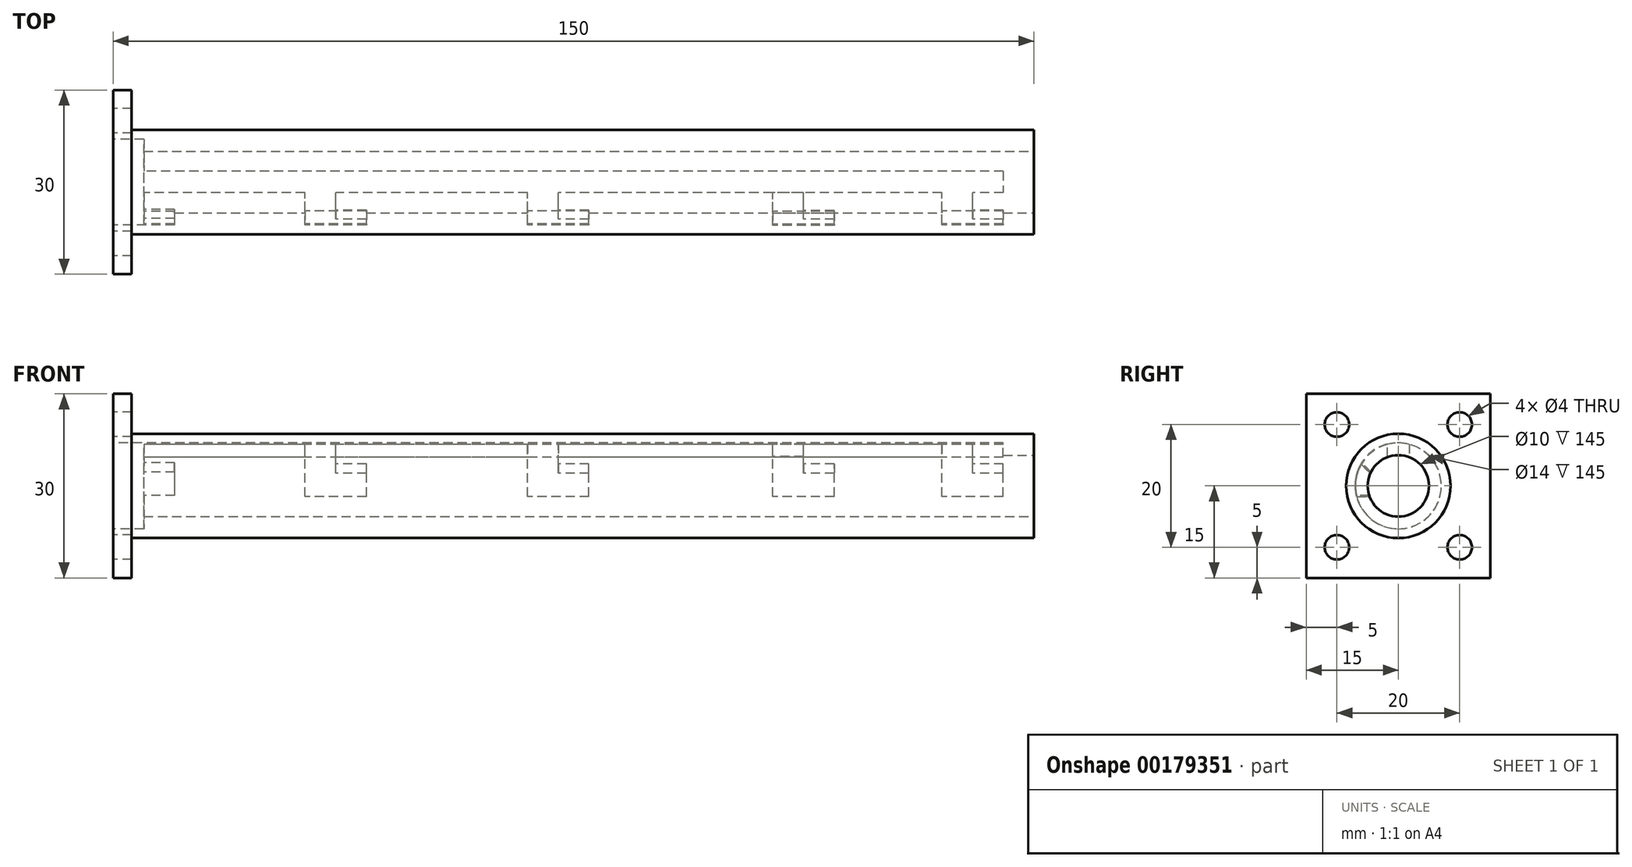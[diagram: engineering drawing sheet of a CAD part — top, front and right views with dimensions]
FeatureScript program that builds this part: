
annotation { "Feature Type Name" : "Feature", "Feature Type Description" : "" }
export const myFeature = defineFeature(function(context is Context, id is Id, definition is map)
    precondition{}
    {
        {
            var Q0;
            Q0=qCreatedBy(makeId("Right.planeOp"),FACE);
            var sketch = newSketch(context, id + "F0", { "sketchPlane" : qUnion([Q0])});
            skCircle(sketch, "E0", {"center": v(0, 0) * mm, "radius": 8.5 * mm});
            skCircle(sketch, "E1", {"center": v(0, 0) * mm, "radius": 7 * mm});
            skSolve(sketch);
        }
        {
            var Q0;
            Q0=makeQuery(id+"F0.imprint","IMPRINT",FACE,{"disambiguationData":[TD([[makeQuery(id+"F0.imprint","IMPRINT",EDGE,{"derivedFrom":sQuery(id+"F0.wireOp",EDGE,"E0")}),1.0]])]});
            extrude(context, id + "F1", {"entities" : qUnion([Q0]), "depth" : 150 * mm});
        }
        {
            var Q0;
            Q0=makeQuery(id+"F1.opExtrude","CAP_FACE",FACE,{"disambiguationData":[OSD([sQuery(id+"F0.wireOp",EDGE,"E0"),sQuery(id+"F0.wireOp",EDGE,"E1")])],"isStart":false});
            var sketch = newSketch(context, id + "F2", { "sketchPlane" : qUnion([Q0])});
            skCircle(sketch, "E2", {"center": v(0, 0) * mm, "radius": 5 * mm});
            skSolve(sketch);
        }
        {
            var Q0;
            Q0=makeQuery(id+"F2.imprint","IMPRINT",FACE,{"disambiguationData":[TD([[makeQuery(id+"F2.imprint","IMPRINT",EDGE,{"derivedFrom":sQuery(id+"F2.wireOp",EDGE,"E2")}),-1.0]])]});
            extrude(context, id + "F3", {"entities" : qUnion([Q0]), "operationType" : NewBodyOperationType.ADD, "oppositeDirection" : true, "depth" : 145 * mm});
        }
        {
            var Q0;
            Q0=makeQuery(id+"F1.opExtrude","CAP_FACE",FACE,{"disambiguationData":[OSD([sQuery(id+"F0.wireOp",EDGE,"E0"),sQuery(id+"F0.wireOp",EDGE,"E1")])],"isStart":true});
            var sketch = newSketch(context, id + "F4", { "sketchPlane" : qUnion([Q0])});
            skLineSegment(sketch, "E3.bottom", {"start": v(15, -15) * mm, "end": v(-15, -15) * mm});
            skLineSegment(sketch, "E3.top", {"start": v(15, 15) * mm, "end": v(-15, 15) * mm});
            skLineSegment(sketch, "E3.left", {"start": v(15, -15) * mm, "end": v(15, 15) * mm});
            skLineSegment(sketch, "E3.right", {"start": v(-15, -15) * mm, "end": v(-15, 15) * mm});
            skPoint(sketch, "E3.middle", {"position": v(0, 0) * mm});
            skSolve(sketch);
        }
        {
            var Q0;
            Q0=makeQuery(id+"F4.imprint","IMPRINT",FACE,{"disambiguationData":[TD([[makeQuery(id+"F4.imprint","IMPRINT",EDGE,{"derivedFrom":sQuery(id+"F4.wireOp",EDGE,"E3.bottom")}),-1.0]])]});
            extrude(context, id + "F5", {"entities" : qUnion([Q0]), "operationType" : NewBodyOperationType.ADD, "oppositeDirection" : true, "depth" : 3 * mm});
        }
        {
            var Q0;
            {var subQ0=sQuery(id+"F0.wireOp",EDGE,"E0");Q0=makeQuery(id+"F5.boolean.opBoolean","MERGE",FACE,{"derivedFrom":[makeQuery(id+"F1.opExtrude","CAP_FACE",FACE,{"disambiguationData":[OSD([subQ0,sQuery(id+"F0.wireOp",EDGE,"E1")])],"isStart":true}),makeQuery(id+"F5.opExtrude","CAP_FACE",FACE,{"disambiguationData":[OSD([subQ0,sQuery(id+"F4.wireOp",EDGE,"E3.bottom"),sQuery(id+"F4.wireOp",EDGE,"E3.top"),sQuery(id+"F4.wireOp",EDGE,"E3.left"),sQuery(id+"F4.wireOp",EDGE,"E3.right")])],"isStart":true})]});}
            var sketch = newSketch(context, id + "F6", { "sketchPlane" : qUnion([Q0])});
            skPoint(sketch, "E4", {"position": v(0, 15) * mm});
            skPoint(sketch, "E5", {"position": v(-15, 0) * mm});
            skPoint(sketch, "E6", {"position": v(0, -15) * mm});
            skPoint(sketch, "E7", {"position": v(15, 0) * mm});
            skPoint(sketch, "E8", {"position": v(-10, 10) * mm});
            skPoint(sketch, "E9", {"position": v(10, 10) * mm});
            skPoint(sketch, "E10", {"position": v(10, -10) * mm});
            skPoint(sketch, "E11", {"position": v(-10, -10) * mm});
            skSolve(sketch);
        }
        {
            var Q0;
            Q0=sQuery(id+"F6.wireOp",VERTEX,"E8");
            var Q1;
            Q1=sQuery(id+"F6.wireOp",VERTEX,"E9");
            var Q2;
            Q2=sQuery(id+"F6.wireOp",VERTEX,"E10");
            var Q3;
            Q3=sQuery(id+"F6.wireOp",VERTEX,"E11");
            var Q4;
            Q4=makeQuery(id+"F1.opExtrude","SWEPT_BODY",BODY,{"disambiguationData":[OSD([sQuery(id+"F0.wireOp",EDGE,"E0"),sQuery(id+"F0.wireOp",EDGE,"E1")])]});
            hole(context, id + "F7", {"style" : HoleStyle.SIMPLE, "endStyle" : HoleEndStyle.THROUGH, "holeDiameter" : 4 * mm, "locations" : qUnion([Q0, Q1, Q2, Q3]), "scope" : qUnion([Q4]), "isTappedThrough" : true});
        }
        {
            var Q0;
            Q0=makeQuery(id+"F3.opExtrude","CAP_FACE",FACE,{"disambiguationData":[OSD([sQuery(id+"F0.wireOp",EDGE,"E1"),sQuery(id+"F2.wireOp",EDGE,"E2")])],"isStart":false});
            var sketch = newSketch(context, id + "F8", { "sketchPlane" : qUnion([Q0])});
            skLineSegment(sketch, "E12", {"start": v(1.75, 4.68) * mm, "end": v(1.75, 6.78) * mm});
            skLineSegment(sketch, "E13", {"start": v(-1.75, 6.78) * mm, "end": v(-1.75, 4.68) * mm});
            skLineSegment(sketch, "E14", {"start": v(0, 5) * mm, "end": v(0, 7) * mm});
            skSolve(sketch);
        }
        {
            var Q0;
            {var subQ0=sQuery(id+"F8.wireOp",EDGE,"E12");Q0=makeQuery(id+"F8.imprint","IMPRINT",FACE,{"disambiguationData":[TD([[makeQuery(id+"F8.imprint","IMPRINT",EDGE,{"derivedFrom":subQ0}),1.0]])]});}
            var Q1;
            {var subQ0=sQuery(id+"F8.wireOp",EDGE,"E13");Q1=makeQuery(id+"F8.imprint","IMPRINT",FACE,{"disambiguationData":[TD([[makeQuery(id+"F8.imprint","IMPRINT",EDGE,{"derivedFrom":subQ0}),1.0]])]});}
            extrude(context, id + "F9", {"entities" : qUnion([Q0, Q1]), "operationType" : NewBodyOperationType.REMOVE, "oppositeDirection" : true, "depth" : 140 * mm});
        }
        {
            var Q0;
            Q0=makeQuery(id+"F9.boolean.opBoolean","COPY",FACE,{"derivedFrom":makeQuery(id+"F9.opExtrude","SWEPT_FACE",FACE,{"disambiguationData":[OSD([sQuery(id+"F8.wireOp",EDGE,"E12")])]})});
            var sketch = newSketch(context, id + "F10", { "sketchPlane" : qUnion([Q0])});
            skLineSegment(sketch, "E15.right", {"start": v(-140, 4.7) * mm, "end": v(-140, 6.78) * mm});
            skLineSegment(sketch, "E16.bottom", {"start": v(-140, 6.78) * mm, "end": v(-135, 6.78) * mm});
            skLineSegment(sketch, "E16.top", {"start": v(-140, 4.68) * mm, "end": v(-135, 4.68) * mm});
            skLineSegment(sketch, "E16.left", {"start": v(-140, 6.78) * mm, "end": v(-140, 4.68) * mm});
            skLineSegment(sketch, "E16.right", {"start": v(-135, 6.78) * mm, "end": v(-135, 4.68) * mm});
            skSolve(sketch);
        }
        {
            var Q0;
            Q0=qCreatedBy(makeId("Top.planeOp"),FACE);
            var sketch = newSketch(context, id + "F11", { "sketchPlane" : qUnion([Q0])});
            skLineSegment(sketch, "E17", {"start": v(0, 0) * mm, "end": v(149.97, 0) * mm});
            skPoint(sketch, "E18", {"position": v(74.99, 0) * mm});
            skLineSegment(sketch, "E19", {"start": v(74.99, 0) * mm, "end": v(149.97, 0) * mm});
            skLineSegment(sketch, "E20", {"start": v(74.99, 0) * mm, "end": v(0, 0) * mm});
            skPoint(sketch, "E21", {"position": v(37.5, 0) * mm});
            skPoint(sketch, "E22", {"position": v(112.48, 0) * mm});
            skSolve(sketch);
        }
        {
            var Q0;
            Q0 = qSketchRegion(id + "F10", true);
            var Q1;
            Q1=sQuery(id+"F11.wireOp",EDGE,"E17");
            revolve(context, id + "F12", {"operationType" : NewBodyOperationType.REMOVE, "entities" : qUnion([Q0]), "axis" : qUnion([Q1]), "revolveType" : RevolveType.ONE_DIRECTION, "angle" : 90 * degree});
        }
        {
            var Q0;
            Q0=makeQuery(id+"F12.boolean.opBoolean","COPY",FACE,{"derivedFrom":makeQuery(id+"F12.opRevolve","SWEPT_FACE",FACE,{"disambiguationData":[OSD([sQuery(id+"F10.wireOp",EDGE,"E16.left")])]})});
            var sketch = newSketch(context, id + "F13", { "sketchPlane" : qUnion([Q0])});
            skLineSegment(sketch, "E23", {"start": v(4.55, 2.07) * mm, "end": v(6.03, 3.56) * mm});
            skSolve(sketch);
        }
        {
            var Q0;
            {var subQ0=sQuery(id+"F13.wireOp",EDGE,"E23");Q0=makeQuery(id+"F13.imprint","IMPRINT",FACE,{"disambiguationData":[TD([[makeQuery(id+"F13.imprint","IMPRINT",EDGE,{"derivedFrom":subQ0}),-1.0]])]});}
            extrude(context, id + "F14", {"entities" : qUnion([Q0]), "operationType" : NewBodyOperationType.REMOVE, "oppositeDirection" : true, "depth" : 5 * mm});
        }
        {
            var Q0;
            Q0=makeQuery(id+"F9.boolean.opBoolean","COPY",FACE,{"derivedFrom":makeQuery(id+"F9.opExtrude","SWEPT_FACE",FACE,{"disambiguationData":[OSD([sQuery(id+"F8.wireOp",EDGE,"E12")])]})});
            var sketch = newSketch(context, id + "F15", { "sketchPlane" : qUnion([Q0])});
            skLineSegment(sketch, "E24", {"start": v(-70, 6.78) * mm, "end": v(-70, 4.68) * mm});
            skLineSegment(sketch, "E25.bottom", {"start": v(-67.5, 6.78) * mm, "end": v(-72.5, 6.78) * mm});
            skLineSegment(sketch, "E25.top", {"start": v(-67.5, 4.68) * mm, "end": v(-72.5, 4.68) * mm});
            skLineSegment(sketch, "E25.left", {"start": v(-67.5, 6.78) * mm, "end": v(-67.5, 4.68) * mm});
            skLineSegment(sketch, "E25.right", {"start": v(-72.5, 6.78) * mm, "end": v(-72.5, 4.68) * mm});
            skPoint(sketch, "E25.middle", {"position": v(-70, 5.73) * mm});
            skSolve(sketch);
        }
        {
            var Q0;
            Q0 = qSketchRegion(id + "F15", true);
            var Q1;
            Q1=sQuery(id+"F11.wireOp",EDGE,"E17");
            revolve(context, id + "F16", {"operationType" : NewBodyOperationType.REMOVE, "entities" : qUnion([Q0]), "axis" : qUnion([Q1]), "revolveType" : RevolveType.ONE_DIRECTION, "angle" : 90 * degree});
        }
        {
            var Q0;
            Q0=makeQuery(id+"F16.boolean.opBoolean","COPY",FACE,{"derivedFrom":makeQuery(id+"F16.opRevolve","SWEPT_FACE",FACE,{"disambiguationData":[OSD([sQuery(id+"F15.wireOp",EDGE,"E25.left")])]})});
            var sketch = newSketch(context, id + "F17", { "sketchPlane" : qUnion([Q0])});
            skLineSegment(sketch, "E26", {"start": v(-4.55, 2.07) * mm, "end": v(-6.03, 3.56) * mm});
            skSolve(sketch);
        }
        {
            var Q0;
            {var subQ0=sQuery(id+"F17.wireOp",EDGE,"E26");Q0=makeQuery(id+"F17.imprint","IMPRINT",FACE,{"disambiguationData":[TD([[makeQuery(id+"F17.imprint","IMPRINT",EDGE,{"derivedFrom":subQ0}),1.0]])]});}
            extrude(context, id + "F18", {"entities" : qUnion([Q0]), "operationType" : NewBodyOperationType.REMOVE, "depth" : 10 * mm});
        }
        {
            var Q0;
            {var subQ2=sQuery(id+"F8.wireOp",EDGE,"E12");var subQ8=makeQuery(id+"F12.opRevolve","SWEPT_FACE",FACE,{"disambiguationData":[OSD([sQuery(id+"F10.wireOp",EDGE,"E16.right")])]});Q0=makeQuery(id+"F16.boolean.opBoolean","SPLIT",FACE,{"disambiguationData":[TD([makeQuery(id+"F12.boolean.opBoolean","COPY",FACE,{"derivedFrom":subQ8})])],"derivedFrom":makeQuery(id+"F12.boolean.opBoolean","SPLIT",FACE,{"disambiguationData":[TD([subQ8])],"derivedFrom":makeQuery(id+"F9.boolean.opBoolean","COPY",FACE,{"derivedFrom":makeQuery(id+"F9.opExtrude","SWEPT_FACE",FACE,{"disambiguationData":[OSD([subQ2])]})})})});}
            var sketch = newSketch(context, id + "F19", { "sketchPlane" : qUnion([Q0])});
            skLineSegment(sketch, "E27.bottom", {"start": v(-112.45, 4.77) * mm, "end": v(-107.45, 4.77) * mm});
            skLineSegment(sketch, "E27.top", {"start": v(-112.45, 6.84) * mm, "end": v(-107.45, 6.84) * mm});
            skLineSegment(sketch, "E27.right", {"start": v(-107.45, 4.77) * mm, "end": v(-107.45, 6.84) * mm});
            skLineSegment(sketch, "E28.left", {"start": v(-112.45, 4.77) * mm, "end": v(-112.45, 6.84) * mm});
            skSolve(sketch);
        }
        {
            var Q0;
            Q0 = qSketchRegion(id + "F19", true);
            var Q1;
            Q1=sQuery(id+"F11.wireOp",EDGE,"E19");
            revolve(context, id + "F20", {"operationType" : NewBodyOperationType.REMOVE, "entities" : qUnion([Q0]), "axis" : qUnion([Q1]), "revolveType" : RevolveType.ONE_DIRECTION, "angle" : 90 * degree});
        }
        {
            var Q0;
            Q0=makeQuery(id+"F20.boolean.opBoolean","COPY",FACE,{"derivedFrom":makeQuery(id+"F20.opRevolve","SWEPT_FACE",FACE,{"disambiguationData":[OSD([sQuery(id+"F19.wireOp",EDGE,"E28.left")])]})});
            var sketch = newSketch(context, id + "F21", { "sketchPlane" : qUnion([Q0])});
            skLineSegment(sketch, "E29", {"start": v(6.07, 3.6) * mm, "end": v(4.64, 2.07) * mm});
            skSolve(sketch);
        }
        {
            var Q0;
            {var subQ0=sQuery(id+"F21.wireOp",EDGE,"E29");Q0=makeQuery(id+"F21.imprint","IMPRINT",FACE,{"disambiguationData":[TD([[makeQuery(id+"F21.imprint","IMPRINT",EDGE,{"derivedFrom":subQ0}),1.0]])]});}
            extrude(context, id + "F22", {"entities" : qUnion([Q0]), "operationType" : NewBodyOperationType.REMOVE, "oppositeDirection" : true, "depth" : 5 * mm});
        }
        {
            var Q0;
            {var subQ3=sQuery(id+"F8.wireOp",EDGE,"E12");Q0=makeQuery(id+"F16.boolean.opBoolean","SPLIT",FACE,{"disambiguationData":[TD([makeQuery(id+"F16.opRevolve","SWEPT_FACE",FACE,{"disambiguationData":[OSD([sQuery(id+"F15.wireOp",EDGE,"E25.left")])]})])],"derivedFrom":makeQuery(id+"F9.boolean.opBoolean","COPY",FACE,{"derivedFrom":makeQuery(id+"F9.opExtrude","SWEPT_FACE",FACE,{"disambiguationData":[OSD([subQ3])]})})});}
            var sketch = newSketch(context, id + "F23", { "sketchPlane" : qUnion([Q0])});
            skLineSegment(sketch, "E30.bottom", {"start": v(-36.25, 4.68) * mm, "end": v(-31.25, 4.68) * mm});
            skLineSegment(sketch, "E30.top", {"start": v(-36.25, 6.78) * mm, "end": v(-31.25, 6.78) * mm});
            skLineSegment(sketch, "E30.left", {"start": v(-36.25, 4.68) * mm, "end": v(-36.25, 6.78) * mm});
            skLineSegment(sketch, "E30.right", {"start": v(-31.25, 4.68) * mm, "end": v(-31.25, 6.78) * mm});
            skSolve(sketch);
        }
        {
            var Q0;
            Q0=makeQuery(id+"F23.imprint","IMPRINT",FACE,{"disambiguationData":[TD([[makeQuery(id+"F23.imprint","IMPRINT",EDGE,{"derivedFrom":sQuery(id+"F23.wireOp",EDGE,"E30.bottom")}),1.0]])]});
            var Q1;
            Q1=sQuery(id+"F11.wireOp",EDGE,"E17");
            revolve(context, id + "F24", {"operationType" : NewBodyOperationType.REMOVE, "entities" : qUnion([Q0]), "axis" : qUnion([Q1]), "revolveType" : RevolveType.ONE_DIRECTION, "angle" : 90 * degree});
        }
        {
            var Q0;
            Q0=makeQuery(id+"F24.boolean.opBoolean","COPY",FACE,{"derivedFrom":makeQuery(id+"F24.opRevolve","SWEPT_FACE",FACE,{"disambiguationData":[OSD([sQuery(id+"F23.wireOp",EDGE,"E30.right")])]})});
            var sketch = newSketch(context, id + "F25", { "sketchPlane" : qUnion([Q0])});
            skLineSegment(sketch, "E31", {"start": v(-4.55, 2.07) * mm, "end": v(-6.03, 3.56) * mm});
            skSolve(sketch);
        }
        {
            var Q0;
            {var subQ0=sQuery(id+"F25.wireOp",EDGE,"E31");Q0=makeQuery(id+"F25.imprint","IMPRINT",FACE,{"disambiguationData":[TD([[makeQuery(id+"F25.imprint","IMPRINT",EDGE,{"derivedFrom":subQ0}),1.0]])]});}
            extrude(context, id + "F26", {"entities" : qUnion([Q0]), "operationType" : NewBodyOperationType.REMOVE, "depth" : 10 * mm});
        }
        {
            var Q0;
            {var subQ2=sQuery(id+"F15.wireOp",EDGE,"E25.left");var subQ3=sQuery(id+"F8.wireOp",EDGE,"E12");Q0=makeQuery(id+"F24.boolean.opBoolean","SPLIT",FACE,{"disambiguationData":[TD([makeQuery(id+"F24.opRevolve","SWEPT_FACE",FACE,{"disambiguationData":[OSD([sQuery(id+"F23.wireOp",EDGE,"E30.right")])]})])],"derivedFrom":makeQuery(id+"F16.boolean.opBoolean","SPLIT",FACE,{"disambiguationData":[TD([makeQuery(id+"F16.opRevolve","SWEPT_FACE",FACE,{"disambiguationData":[OSD([subQ2])]})])],"derivedFrom":makeQuery(id+"F12.boolean.opBoolean","SPLIT",FACE,{"disambiguationData":[TD([makeQuery(id+"F12.opRevolve","SWEPT_FACE",FACE,{"disambiguationData":[OSD([sQuery(id+"F10.wireOp",EDGE,"E16.right")])]})])],"derivedFrom":makeQuery(id+"F9.boolean.opBoolean","COPY",FACE,{"derivedFrom":makeQuery(id+"F9.opExtrude","SWEPT_FACE",FACE,{"disambiguationData":[OSD([subQ3])]})})})})});}
            var sketch = newSketch(context, id + "F27", { "sketchPlane" : qUnion([Q0])});
            skLineSegment(sketch, "E32.bottom", {"start": v(-5, 4.68) * mm, "end": v(-10, 4.68) * mm});
            skLineSegment(sketch, "E32.top", {"start": v(-5, 6.78) * mm, "end": v(-10, 6.78) * mm});
            skLineSegment(sketch, "E32.left", {"start": v(-5, 4.68) * mm, "end": v(-5, 6.78) * mm});
            skLineSegment(sketch, "E32.right", {"start": v(-10, 4.68) * mm, "end": v(-10, 6.78) * mm});
            skSolve(sketch);
        }
        {
            var Q0;
            Q0 = qSketchRegion(id + "F27", true);
            var Q1;
            Q1=sQuery(id+"F11.wireOp",EDGE,"E17");
            revolve(context, id + "F28", {"operationType" : NewBodyOperationType.ADD, "entities" : qUnion([Q0]), "axis" : qUnion([Q1]), "revolveType" : RevolveType.ONE_DIRECTION, "angle" : 90 * degree});
        }
        {
            var Q0;
            Q0=makeQuery(id+"F3.opExtrude","CAP_FACE",FACE,{"disambiguationData":[OSD([sQuery(id+"F0.wireOp",EDGE,"E1"),sQuery(id+"F2.wireOp",EDGE,"E2")])],"isStart":false});
            var sketch = newSketch(context, id + "F29", { "sketchPlane" : qUnion([Q0])});
            skPoint(sketch, "E33", {"position": v(5, 0) * mm});
            skLineSegment(sketch, "E34", {"start": v(4.47, 2.24) * mm, "end": v(5.9, 3.77) * mm});
            skLineSegment(sketch, "E35", {"start": v(4.74, -1.59) * mm, "end": v(6.82, -1.59) * mm});
            skSolve(sketch);
        }
        {
            var Q0;
            {var subQ0=sQuery(id+"F29.wireOp",EDGE,"E34");Q0=makeQuery(id+"F29.imprint","IMPRINT",FACE,{"disambiguationData":[TD([[makeQuery(id+"F29.imprint","IMPRINT",EDGE,{"derivedFrom":subQ0}),-1.0]])]});}
            extrude(context, id + "F30", {"entities" : qUnion([Q0]), "operationType" : NewBodyOperationType.REMOVE, "oppositeDirection" : true, "depth" : 5 * mm});
        }
    });
